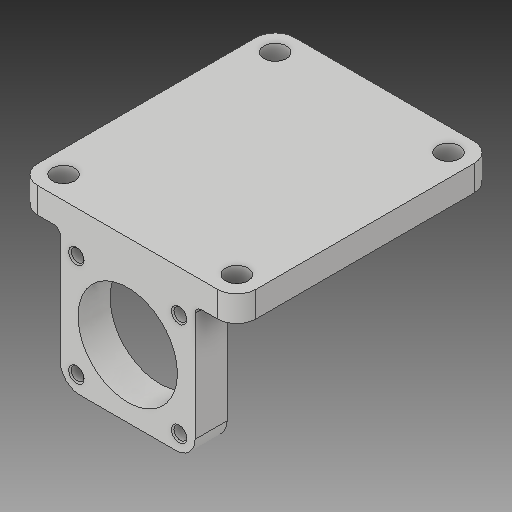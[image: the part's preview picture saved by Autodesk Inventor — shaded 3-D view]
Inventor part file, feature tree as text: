
AUTODESK INVENTOR PART (.ipt)
format: ipt  version: 2019 (Build 230136000, 136)  size: 196,096 bytes
history: native  units: mm
features: fillet x4, extrude x2, chamfer x2, sketch x2
ambient origin geometry x8: Origin, YZ Plane, XZ Plane, XY Plane, X Axis, Y Axis, Z Axis, Center Point
bodies: Solid1 (feature_tree)
feature tree (10):
  extrude  "Extrusion1"  Depth=16.0mm
  extrude  "Extrusion2"  Depth=21.0mm
  fillet  "Fillet2"  Radius=21.0mm
  fillet  "Fillet3"  Radius=2.0mm
  fillet  "Fillet4"  Radius=40.0mm
  chamfer  "Chamfer1"  Distance=5.0mm
  fillet  "Fillet5"  Radius=17.0mm
  chamfer  "Chamfer2"  Distance=5.0mm
  sketch  "Sketch1"  dims[d0=16.0mm d1=16.0mm]
  sketch  "Sketch2"  dims[d2=15.5mm d3=21.0mm d4=21.0mm d5=2.0mm d6=40.0mm d8=360.0deg d10=5.0mm d11=0.0mm d12=17.0mm d13=5.0mm d14=34.0mm d15=40.0mm d16=27.0mm d17=33.0mm d18=3.5mm d19=3.5mm d20=3.5mm d21=3.5mm d22=4.0mm d23=0.0mm d25=3.0mm d26=3.0mm d27=0.4mm d28=0.2mm d29=2.0mm d30=45.0deg d31=1.0mm d32=0.2mm d33=2.0mm d34=45.0deg]
